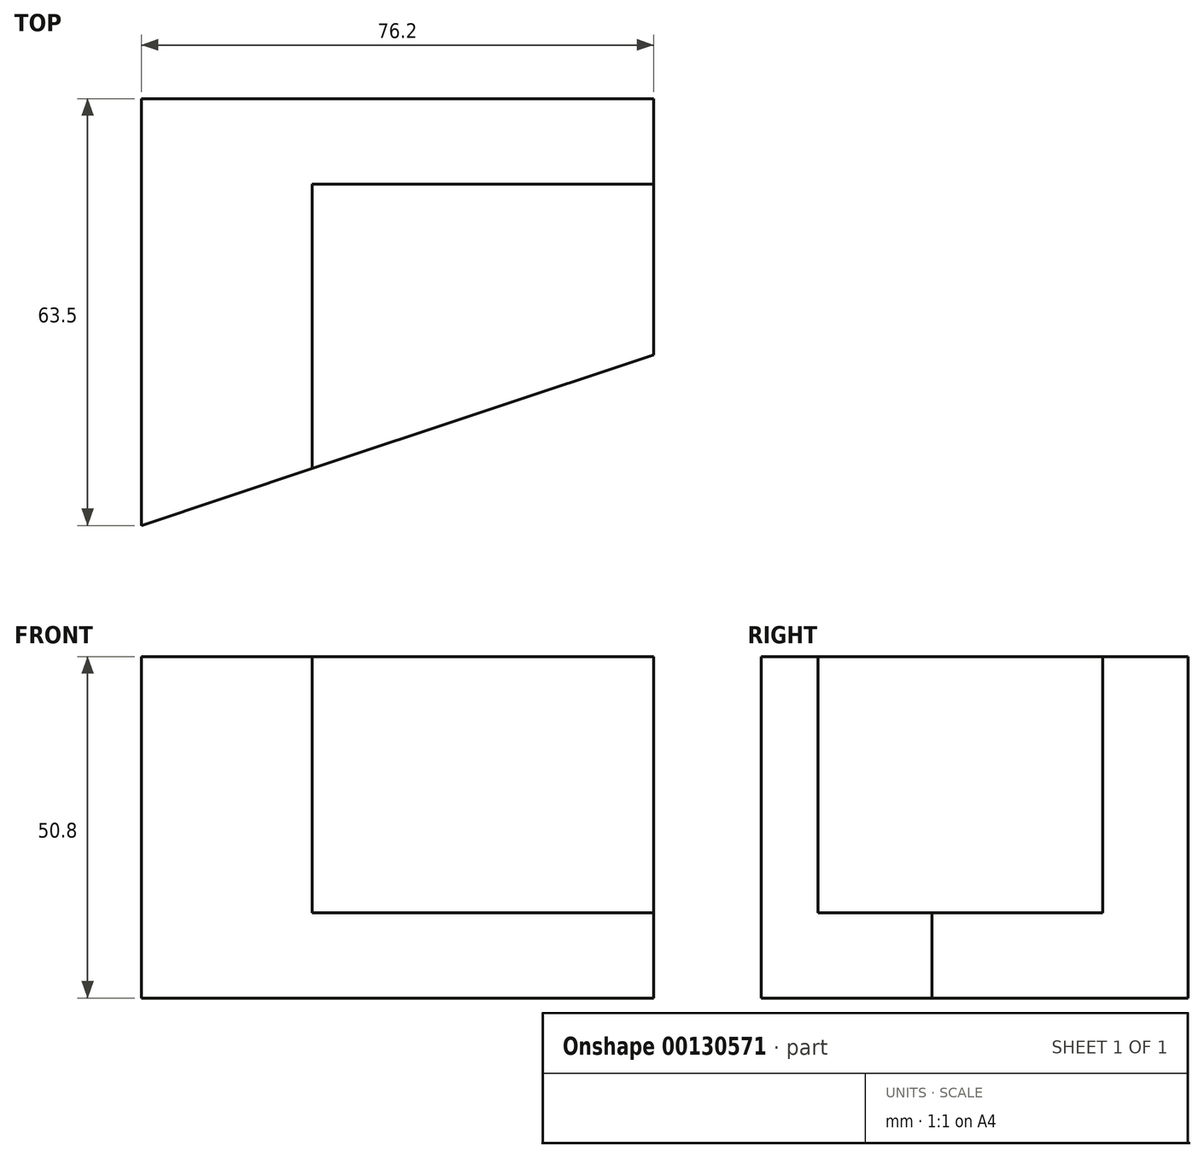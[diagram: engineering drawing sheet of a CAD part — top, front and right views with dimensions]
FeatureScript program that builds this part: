
annotation { "Feature Type Name" : "Feature", "Feature Type Description" : "" }
export const myFeature = defineFeature(function(context is Context, id is Id, definition is map)
    precondition{}
    {
        {
            var Q0;
            Q0=qCreatedBy(makeId("Top.planeOp"),FACE);
            var sketch = newSketch(context, id + "F0", { "sketchPlane" : qUnion([Q0])});
            skLineSegment(sketch, "E0", {"start": v(0, 0) * mm, "end": v(76.2, 0) * mm});
            skLineSegment(sketch, "E1", {"start": v(76.2, 0) * mm, "end": v(76.2, -12.7) * mm});
            skLineSegment(sketch, "E2", {"start": v(76.2, -12.7) * mm, "end": v(25.4, -12.7) * mm});
            skLineSegment(sketch, "E3", {"start": v(25.4, -12.7) * mm, "end": v(25.4, -55.03) * mm});
            skLineSegment(sketch, "E4", {"start": v(0, -63.5) * mm, "end": v(0, 0) * mm});
            skLineSegment(sketch, "E5", {"start": v(76.2, -38.1) * mm, "end": v(76.2, -12.7) * mm});
            skLineSegment(sketch, "E6", {"start": v(0, -63.5) * mm, "end": v(76.2, -38.1) * mm});
            skSolve(sketch);
        }
        {
            var Q0;
            Q0=makeQuery(id+"F0.imprint","IMPRINT",FACE,{"disambiguationData":[TD([[makeQuery(id+"F0.imprint","IMPRINT",EDGE,{"derivedFrom":sQuery(id+"F0.wireOp",EDGE,"E0")}),-1.0]])]});
            extrude(context, id + "F1", {"entities" : qUnion([Q0]), "depth" : 50.8 * mm});
        }
        {
            var Q0;
            Q0=makeQuery(id+"F0.imprint","IMPRINT",FACE,{"disambiguationData":[TD([[makeQuery(id+"F0.imprint","IMPRINT",EDGE,{"derivedFrom":sQuery(id+"F0.wireOp",EDGE,"E2")}),1.0]])]});
            extrude(context, id + "F2", {"entities" : qUnion([Q0]), "operationType" : NewBodyOperationType.ADD, "depth" : 12.7 * mm});
        }
    });
